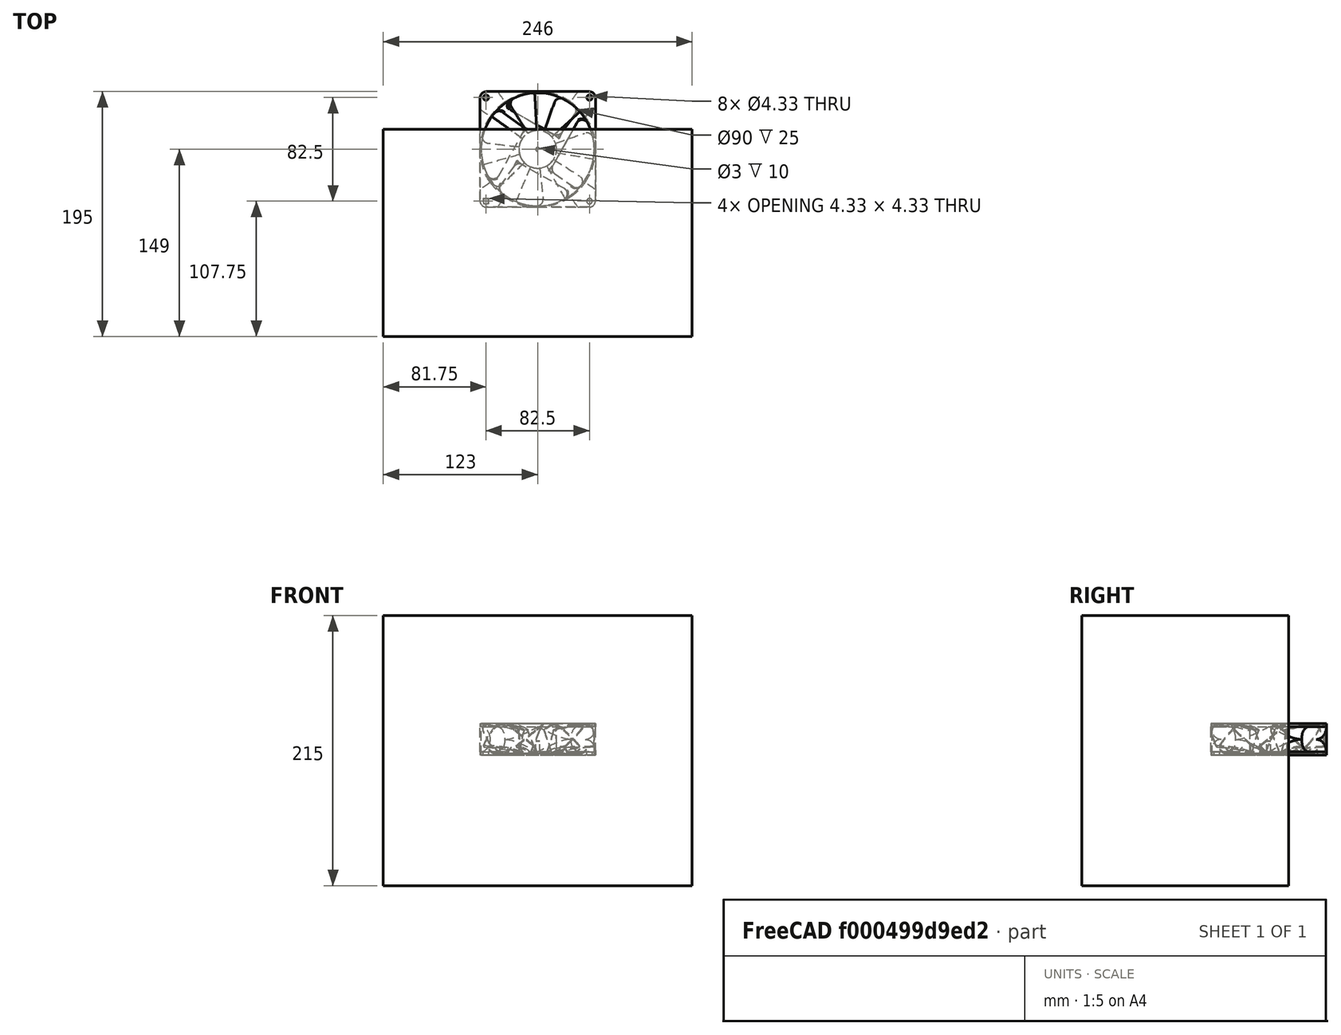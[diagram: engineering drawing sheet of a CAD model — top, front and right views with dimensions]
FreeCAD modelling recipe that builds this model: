
FCSTD DOCUMENT  (FreeCAD 0.21R33668 +7 (Git))
Label: Odroid_h4_mount_CAR_July_15_2024
License: All rights reserved
LicenseURL: https://en.wikipedia.org/wiki/All_rights_reserved
objects: Part::Box×81, Part::MultiFuse×38, Part::Cylinder×30, Part::Cut×6, Part::Feature×3, Part::Fillet×3, App::Part×2, Mesh::Feature×1
note: 161 computed .brp shape members not serialized (recipe doc carries the construction recipe); baked Part::Feature solids carry a one-line shape summary decoded from their .brp

FEATURE [Part::Feature] Part__Feature  label="fan form"
  shape: bbox 105.3 x 105.3 x 25.46 mm, 118 faces (baked)
FEATURE [Part::Feature] Part__Feature001  label="fan"
  Placement = pos=(0,0,1.25) rot=(0,0,-1;0.171016rad)
  shape: bbox 91.23 x 90.98 x 28.5 mm, 54 faces (baked)
FEATURE [App::Part] Assem1  label="Fan"
  Group = -> [Part__Feature,Part__Feature001]
  Origin = -> Origin
  Placement = pos=(0,-5.5,0) rot=(1,0,0;1.5708rad)
FEATURE [Part::Box] Box  label="Base_Plate"
  AttacherType = Attacher::AttachEngine3D
  Height = 45
  Length = 152
  Placement = pos=(76,6,-57) rot=(0,0.707107,-0.707107;3.14159rad)
  Width = 15
FEATURE [Part::Box] Box001  label="Cube001"
  AttacherType = Attacher::AttachEngine3D
  Height = 118
  Length = 11
  Placement = pos=(65,0,-57) rot=(0,0,1;0rad)
  Width = 6
FEATURE [Part::Box] Box002  label="Cube002"
  AttacherType = Attacher::AttachEngine3D
  Height = 118
  Length = 11
  Placement = pos=(-76,0,-57) rot=(0,0,1;0rad)
  Width = 6
FEATURE [Part::Feature] Part__Feature002  label="Fan_mount"
  Placement = pos=(0,0,0) rot=(-1,0,0;1.5708rad)
  shape: bbox 152 x 14.25 x 122 mm, 73 faces (baked)
FEATURE [Part::MultiFuse] Fusion  label="Base"
  Shapes = -> [Box,Box001,Box002]
FEATURE [Part::Fillet] Fillet  label="Fan_hold"
  Base = -> Fusion
  Edges = 2 edges r=2.5: [Edge7,Edge36]
FEATURE [Part::Box] Box003  label="Volume "
  AttacherType = Attacher::AttachEngine3D
  Height = 165
  Length = 246
  Placement = pos=(123,16,111) rot=(0,0.707107,-0.707107;3.14159rad)
  Width = 215
FEATURE [Mesh::Feature] Odroid_H004  label="Odroid-H004"
  Placement = pos=(-50,-110,62) rot=(1,0,0;4.71239rad)
FEATURE [Part::Box] Box004  label="Base_Plate001"
  AttacherType = Attacher::AttachEngine3D
  Height = 102
  Length = 152
  Placement = pos=(76,-39,-57) rot=(0,0.707107,-0.707107;3.14159rad)
  Width = 15
FEATURE [Part::Box] Box006  label="Cube003"
  AttacherType = Attacher::AttachEngine3D
  Height = 20
  Length = 10
  Placement = pos=(-35,-60,0) rot=(0,0,1;0.785398rad)
  Width = 10
FEATURE [Part::Box] Box007  label="Cube004"
  AttacherType = Attacher::AttachEngine3D
  Height = 20
  Length = 10
  Placement = pos=(-10,-60,0) rot=(0,0,1;0.785398rad)
  Width = 10
FEATURE [Part::Box] Box008  label="Cube005"
  AttacherType = Attacher::AttachEngine3D
  Height = 20
  Length = 10
  Placement = pos=(15,-60,0) rot=(0,0,1;0.785398rad)
  Width = 10
FEATURE [Part::Box] Box009  label="Cube006"
  AttacherType = Attacher::AttachEngine3D
  Height = 20
  Length = 10
  Placement = pos=(40,-60,0) rot=(0,0,1;0.785398rad)
  Width = 10
FEATURE [Part::Box] Box010  label="Cube007"
  AttacherType = Attacher::AttachEngine3D
  Height = 20
  Length = 10
  Placement = pos=(64,-60,0) rot=(0,0,1;0.785398rad)
  Width = 10
FEATURE [Part::Box] Box011  label="Cube008"
  AttacherType = Attacher::AttachEngine3D
  Height = 20
  Length = 10
  Placement = pos=(-60,-60,0) rot=(0,0,1;0.785398rad)
  Width = 10
FEATURE [Part::Box] Box012  label="Cube009"
  AttacherType = Attacher::AttachEngine3D
  Height = 20
  Length = 10
  Placement = pos=(-35,-60,0) rot=(0,0,1;0.785398rad)
  Width = 10
FEATURE [Part::Box] Box013  label="Cube010"
  AttacherType = Attacher::AttachEngine3D
  Height = 20
  Length = 10
  Placement = pos=(-10,-60,0) rot=(0,0,1;0.785398rad)
  Width = 10
FEATURE [Part::Box] Box014  label="Cube011"
  AttacherType = Attacher::AttachEngine3D
  Height = 20
  Length = 10
  Placement = pos=(15,-60,0) rot=(0,0,1;0.785398rad)
  Width = 10
FEATURE [Part::Box] Box015  label="Cube012"
  AttacherType = Attacher::AttachEngine3D
  Height = 20
  Length = 10
  Placement = pos=(40,-60,0) rot=(0,0,1;0.785398rad)
  Width = 10
FEATURE [Part::MultiFuse] Fusion002  label="CubeLine002"
  Placement = pos=(10,-13,0) rot=(0,0,1;0rad)
  Shapes = -> [Box011,Box012,Box013,Box014,Box015]
FEATURE [Part::Box] Box016  label="Cube013"
  AttacherType = Attacher::AttachEngine3D
  Height = 20
  Length = 10
  Placement = pos=(-60,-60,0) rot=(0,0,1;0.785398rad)
  Width = 10
FEATURE [Part::Box] Box017  label="Cube014"
  AttacherType = Attacher::AttachEngine3D
  Height = 20
  Length = 10
  Placement = pos=(-35,-60,0) rot=(0,0,1;0.785398rad)
  Width = 10
FEATURE [Part::Box] Box018  label="Cube015"
  AttacherType = Attacher::AttachEngine3D
  Height = 20
  Length = 10
  Placement = pos=(-10,-60,0) rot=(0,0,1;0.785398rad)
  Width = 10
FEATURE [Part::Box] Box019  label="Cube016"
  AttacherType = Attacher::AttachEngine3D
  Height = 20
  Length = 10
  Placement = pos=(15,-60,0) rot=(0,0,1;0.785398rad)
  Width = 10
FEATURE [Part::Box] Box020  label="Cube017"
  AttacherType = Attacher::AttachEngine3D
  Height = 20
  Length = 10
  Placement = pos=(40,-60,0) rot=(0,0,1;0.785398rad)
  Width = 10
FEATURE [Part::Box] Box021  label="Cube018"
  AttacherType = Attacher::AttachEngine3D
  Height = 20
  Length = 10
  Placement = pos=(64,-60,0) rot=(0,0,1;0.785398rad)
  Width = 10
FEATURE [Part::MultiFuse] Fusion003  label="CubeLine003"
  Placement = pos=(-2,-25,0) rot=(0,0,1;0rad)
  Shapes = -> [Box016,Box017,Box018,Box019,Box020,Box021]
FEATURE [Part::Box] Box005  label="Cube"
  AttacherType = Attacher::AttachEngine3D
  Height = 20
  Length = 10
  Placement = pos=(-60,-60,0) rot=(0,0,1;0.785398rad)
  Width = 10
FEATURE [Part::MultiFuse] Fusion001  label="CubeLine1"
  Placement = pos=(-2,0,0) rot=(0,0,1;0rad)
  Shapes = -> [Box005,Box006,Box007,Box008,Box009,Box010]
FEATURE [Part::MultiFuse] Fusion004
  Placement = pos=(0,0,-75) rot=(0,0,1;0rad)
  Shapes = -> [Fusion001,Fusion002,Fusion003]
FEATURE [Part::Cut] Cut  label="BasePlate01"
  Base = -> Box004
  Tool = -> Fusion004
FEATURE [Part::Box] Box022  label="Cube019"
  AttacherType = Attacher::AttachEngine3D
  Height = 118
  Length = 15
  Placement = pos=(49,-141,-57) rot=(0,0,1;0rad)
  Width = 10
FEATURE [Part::Box] Box023  label="Cube020"
  AttacherType = Attacher::AttachEngine3D
  Height = 118
  Length = 15
  Placement = pos=(-54,-141,-57) rot=(0,0,1;0rad)
  Width = 10
FEATURE [Part::MultiFuse] Fusion005  label="Base_H4"
  Shapes = -> [Cut,Box022,Box023]
FEATURE [Part::Cylinder] Cylinder
  Angle = 360
  AttacherType = Attacher::AttachEngine3D
  FirstAngle = 0
  Height = 20
  Placement = pos=(-46.19,-136,44.22) rot=(1,0,0;1.5708rad)
  Radius = 1.75
  SecondAngle = 0
FEATURE [Part::Cylinder] Cylinder001
  Angle = 360
  AttacherType = Attacher::AttachEngine3D
  FirstAngle = 0
  Height = 20
  Placement = pos=(-46.19,-136,-44.19) rot=(1,0,0;1.5708rad)
  Radius = 1.75
  SecondAngle = 0
FEATURE [Part::Cylinder] Cylinder002
  Angle = 360
  AttacherType = Attacher::AttachEngine3D
  FirstAngle = 0
  Height = 20
  Placement = pos=(56.05,-136,-44.2) rot=(1,0,0;1.5708rad)
  Radius = 1.75
  SecondAngle = 0
FEATURE [Part::Cylinder] Cylinder003
  Angle = 360
  AttacherType = Attacher::AttachEngine3D
  FirstAngle = 0
  Height = 20
  Placement = pos=(56.05,-136,37.23) rot=(1,0,0;1.5708rad)
  Radius = 1.75
  SecondAngle = 0
FEATURE [Part::MultiFuse] Fusion006  label="Mount_cut"
  Placement = pos=(0,10,0) rot=(0,0,1;0rad)
  Shapes = -> [Cylinder,Cylinder001,Cylinder002,Cylinder003]
FEATURE [Part::Cut] Cut001  label="h4_mount"
  Base = -> Fusion005
  Tool = -> Fusion006
FEATURE [Part::MultiFuse] Fusion007  label="Mount01"
  Shapes = -> [Cut001,Fillet,Part__Feature002]
FEATURE [Part::Fillet] Fillet001  label="Mount"
  Base = -> Fusion007
  Edges = 17 edges r=1: [Edge182,Edge183,Edge184,Edge187,Edge188,Edge307,Edge308,Edge309,Edge310,Edge314,Edge316,Edge317,Edge318,Edge319,Edge323,Edge461,Edge464]
FEATURE [Part::Cylinder] Cylinder004
  Angle = 360
  AttacherType = Attacher::AttachEngine3D
  FirstAngle = 0
  Height = 30
  Placement = pos=(70,17,54) rot=(1,0,0;1.5708rad)
  Radius = 1.75
  SecondAngle = 0
FEATURE [Part::Cylinder] Cylinder005
  Angle = 360
  AttacherType = Attacher::AttachEngine3D
  FirstAngle = 0
  Height = 30
  Placement = pos=(-70,17,54) rot=(1,0,0;1.5708rad)
  Radius = 1.75
  SecondAngle = 0
FEATURE [Part::Cylinder] Cylinder006
  Angle = 360
  AttacherType = Attacher::AttachEngine3D
  FirstAngle = 0
  Height = 30
  Placement = pos=(70,18,-52) rot=(1,0,0;1.5708rad)
  Radius = 1.75
  SecondAngle = 0
FEATURE [Part::Cylinder] Cylinder007
  Angle = 360
  AttacherType = Attacher::AttachEngine3D
  FirstAngle = 0
  Height = 30
  Placement = pos=(-70,18,-52) rot=(1,0,0;1.5708rad)
  Radius = 1.75
  SecondAngle = 0
FEATURE [Part::MultiFuse] Fusion008  label="m3_mount_Cut"
  Shapes = -> [Cylinder004,Cylinder005,Cylinder006,Cylinder007]
FEATURE [Part::Cylinder] Cylinder008
  Angle = 360
  AttacherType = Attacher::AttachEngine3D
  FirstAngle = 0
  Height = 20
  Placement = pos=(70,17,54) rot=(1,0,0;1.5708rad)
  Radius = 3
  SecondAngle = 0
FEATURE [Part::Cylinder] Cylinder009
  Angle = 360
  AttacherType = Attacher::AttachEngine3D
  FirstAngle = 0
  Height = 20
  Placement = pos=(-70,17,54) rot=(1,0,0;1.5708rad)
  Radius = 3
  SecondAngle = 0
FEATURE [Part::Cylinder] Cylinder010
  Angle = 360
  AttacherType = Attacher::AttachEngine3D
  FirstAngle = 0
  Height = 20
  Placement = pos=(70,18,-52) rot=(1,0,0;1.5708rad)
  Radius = 3
  SecondAngle = 0
FEATURE [Part::Cylinder] Cylinder011
  Angle = 360
  AttacherType = Attacher::AttachEngine3D
  FirstAngle = 0
  Height = 20
  Placement = pos=(-70,18,-52) rot=(1,0,0;1.5708rad)
  Radius = 3
  SecondAngle = 0
FEATURE [Part::MultiFuse] Fusion009  label="m3_mount_support"
  Placement = pos=(0,-6,0) rot=(0,0,1;0rad)
  Shapes = -> [Cylinder008,Cylinder009,Cylinder010,Cylinder011]
FEATURE [Part::MultiFuse] Fusion010  label="Mount002"
  Shapes = -> [Fillet001,Fusion009]
FEATURE [Part::Cut] Cut002  label="Base001"
  Base = -> Fusion010
  Tool = -> Fusion008
FEATURE [Part::Box] Box024  label="Base_Plate002"
  AttacherType = Attacher::AttachEngine3D
  Height = 134
  Length = 147
  Placement = pos=(76,72,6) rot=(0.57735,0.57735,-0.57735;2.0944rad)
  Width = 15
FEATURE [Part::Box] Box025  label="Base_Plate003"
  AttacherType = Attacher::AttachEngine3D
  Height = 134
  Length = 147
  Placement = pos=(-76,72,-141) rot=(0.57735,-0.57735,0.57735;2.0944rad)
  Width = 15
FEATURE [Part::Box] Box027  label="Cube022"
  AttacherType = Attacher::AttachEngine3D
  Height = 20
  Length = 10
  Placement = pos=(-35,-60,0) rot=(0,0,1;0.785398rad)
  Width = 10
FEATURE [Part::Box] Box028  label="Cube023"
  AttacherType = Attacher::AttachEngine3D
  Height = 20
  Length = 10
  Placement = pos=(-10,-60,0) rot=(0,0,1;0.785398rad)
  Width = 10
FEATURE [Part::Box] Box029  label="Cube024"
  AttacherType = Attacher::AttachEngine3D
  Height = 20
  Length = 10
  Placement = pos=(15,-60,0) rot=(0,0,1;0.785398rad)
  Width = 10
FEATURE [Part::Box] Box030  label="Cube025"
  AttacherType = Attacher::AttachEngine3D
  Height = 20
  Length = 10
  Placement = pos=(40,-60,0) rot=(0,0,1;0.785398rad)
  Width = 10
FEATURE [Part::Box] Box032  label="Cube027"
  AttacherType = Attacher::AttachEngine3D
  Height = 20
  Length = 10
  Placement = pos=(-60,-60,0) rot=(0,0,1;0.785398rad)
  Width = 10
FEATURE [Part::Box] Box033  label="Cube028"
  AttacherType = Attacher::AttachEngine3D
  Height = 20
  Length = 10
  Placement = pos=(-35,-60,0) rot=(0,0,1;0.785398rad)
  Width = 10
FEATURE [Part::Box] Box034  label="Cube029"
  AttacherType = Attacher::AttachEngine3D
  Height = 20
  Length = 10
  Placement = pos=(-10,-60,0) rot=(0,0,1;0.785398rad)
  Width = 10
FEATURE [Part::Box] Box035  label="Cube030"
  AttacherType = Attacher::AttachEngine3D
  Height = 20
  Length = 10
  Placement = pos=(15,-60,0) rot=(0,0,1;0.785398rad)
  Width = 10
FEATURE [Part::Box] Box036  label="Cube031"
  AttacherType = Attacher::AttachEngine3D
  Height = 20
  Length = 10
  Placement = pos=(40,-60,0) rot=(0,0,1;0.785398rad)
  Width = 10
FEATURE [Part::Box] Box038  label="Cube033"
  AttacherType = Attacher::AttachEngine3D
  Height = 20
  Length = 10
  Placement = pos=(-35,-60,0) rot=(0,0,1;0.785398rad)
  Width = 10
FEATURE [Part::Box] Box039  label="Cube034"
  AttacherType = Attacher::AttachEngine3D
  Height = 20
  Length = 10
  Placement = pos=(-10,-60,0) rot=(0,0,1;0.785398rad)
  Width = 10
FEATURE [Part::Box] Box040  label="Cube035"
  AttacherType = Attacher::AttachEngine3D
  Height = 20
  Length = 10
  Placement = pos=(15,-60,0) rot=(0,0,1;0.785398rad)
  Width = 10
FEATURE [Part::Box] Box041  label="Cube036"
  AttacherType = Attacher::AttachEngine3D
  Height = 20
  Length = 10
  Placement = pos=(40,-60,0) rot=(0,0,1;0.785398rad)
  Width = 10
FEATURE [Part::MultiFuse] Fusion011  label="CubeLine004"
  Placement = pos=(-2,0,0) rot=(0,0,1;0rad)
  Shapes = -> [Box027,Box028,Box029,Box030]
FEATURE [Part::MultiFuse] Fusion012  label="CubeLine005"
  Placement = pos=(10,-13,0) rot=(0,0,1;0rad)
  Shapes = -> [Box032,Box033,Box034,Box035,Box036]
FEATURE [Part::MultiFuse] Fusion013  label="CubeLine006"
  Placement = pos=(-2,-25,0) rot=(0,0,1;0rad)
  Shapes = -> [Box038,Box039,Box040,Box041]
FEATURE [Part::MultiFuse] Fusion014
  Placement = pos=(94,95,-68) rot=(0,1,0;4.71239rad)
  Shapes = -> [Fusion011,Fusion012,Fusion013]
FEATURE [Part::Box] Box044  label="Cube039"
  AttacherType = Attacher::AttachEngine3D
  Height = 20
  Length = 10
  Placement = pos=(-35,-60,0) rot=(0,0,1;0.785398rad)
  Width = 10
FEATURE [Part::Box] Box045  label="Cube040"
  AttacherType = Attacher::AttachEngine3D
  Height = 20
  Length = 10
  Placement = pos=(-10,-60,0) rot=(0,0,1;0.785398rad)
  Width = 10
FEATURE [Part::Box] Box046  label="Cube041"
  AttacherType = Attacher::AttachEngine3D
  Height = 20
  Length = 10
  Placement = pos=(15,-60,0) rot=(0,0,1;0.785398rad)
  Width = 10
FEATURE [Part::Box] Box047  label="Cube042"
  AttacherType = Attacher::AttachEngine3D
  Height = 20
  Length = 10
  Placement = pos=(40,-60,0) rot=(0,0,1;0.785398rad)
  Width = 10
FEATURE [Part::Box] Box049  label="Cube044"
  AttacherType = Attacher::AttachEngine3D
  Height = 20
  Length = 10
  Placement = pos=(-60,-60,0) rot=(0,0,1;0.785398rad)
  Width = 10
FEATURE [Part::Box] Box050  label="Cube045"
  AttacherType = Attacher::AttachEngine3D
  Height = 20
  Length = 10
  Placement = pos=(-35,-60,0) rot=(0,0,1;0.785398rad)
  Width = 10
FEATURE [Part::Box] Box051  label="Cube046"
  AttacherType = Attacher::AttachEngine3D
  Height = 20
  Length = 10
  Placement = pos=(-10,-60,0) rot=(0,0,1;0.785398rad)
  Width = 10
FEATURE [Part::Box] Box052  label="Cube047"
  AttacherType = Attacher::AttachEngine3D
  Height = 20
  Length = 10
  Placement = pos=(15,-60,0) rot=(0,0,1;0.785398rad)
  Width = 10
FEATURE [Part::Box] Box053  label="Cube048"
  AttacherType = Attacher::AttachEngine3D
  Height = 20
  Length = 10
  Placement = pos=(40,-60,0) rot=(0,0,1;0.785398rad)
  Width = 10
FEATURE [Part::Box] Box055  label="Cube050"
  AttacherType = Attacher::AttachEngine3D
  Height = 20
  Length = 10
  Placement = pos=(-35,-60,0) rot=(0,0,1;0.785398rad)
  Width = 10
FEATURE [Part::Box] Box056  label="Cube051"
  AttacherType = Attacher::AttachEngine3D
  Height = 20
  Length = 10
  Placement = pos=(-10,-60,0) rot=(0,0,1;0.785398rad)
  Width = 10
FEATURE [Part::Box] Box057  label="Cube052"
  AttacherType = Attacher::AttachEngine3D
  Height = 20
  Length = 10
  Placement = pos=(15,-60,0) rot=(0,0,1;0.785398rad)
  Width = 10
FEATURE [Part::Box] Box058  label="Cube053"
  AttacherType = Attacher::AttachEngine3D
  Height = 20
  Length = 10
  Placement = pos=(40,-60,0) rot=(0,0,1;0.785398rad)
  Width = 10
FEATURE [Part::MultiFuse] Fusion015  label="CubeLine007"
  Placement = pos=(-2,0,0) rot=(0,0,1;0rad)
  Shapes = -> [Box044,Box045,Box046,Box047]
FEATURE [Part::MultiFuse] Fusion016  label="CubeLine008"
  Placement = pos=(10,-13,0) rot=(0,0,1;0rad)
  Shapes = -> [Box049,Box050,Box051,Box052,Box053]
FEATURE [Part::MultiFuse] Fusion017  label="CubeLine009"
  Placement = pos=(-2,-25,0) rot=(0,0,1;0rad)
  Shapes = -> [Box055,Box056,Box057,Box058]
FEATURE [Part::MultiFuse] Fusion018
  Placement = pos=(94,45,-68) rot=(0,-1,0;1.5708rad)
  Shapes = -> [Fusion015,Fusion016,Fusion017]
FEATURE [Part::MultiFuse] Fusion019  label="Cube_Cut_Side1"
  Shapes = -> [Fusion014,Fusion018]
FEATURE [Part::Cut] Cut003  label="side1"
  Base = -> Box024
  Placement = pos=(0,0,0) rot=(1,0,0;4.71239rad)
  Tool = -> Fusion019
FEATURE [Part::Box] Box061  label="Cube056"
  AttacherType = Attacher::AttachEngine3D
  Height = 20
  Length = 10
  Placement = pos=(-35,-60,0) rot=(0,0,1;0.785398rad)
  Width = 10
FEATURE [Part::Box] Box062  label="Cube057"
  AttacherType = Attacher::AttachEngine3D
  Height = 20
  Length = 10
  Placement = pos=(-10,-60,0) rot=(0,0,1;0.785398rad)
  Width = 10
FEATURE [Part::Box] Box063  label="Cube058"
  AttacherType = Attacher::AttachEngine3D
  Height = 20
  Length = 10
  Placement = pos=(15,-60,0) rot=(0,0,1;0.785398rad)
  Width = 10
FEATURE [Part::Box] Box064  label="Cube059"
  AttacherType = Attacher::AttachEngine3D
  Height = 20
  Length = 10
  Placement = pos=(40,-60,0) rot=(0,0,1;0.785398rad)
  Width = 10
FEATURE [Part::Box] Box066  label="Cube061"
  AttacherType = Attacher::AttachEngine3D
  Height = 20
  Length = 10
  Placement = pos=(-60,-60,0) rot=(0,0,1;0.785398rad)
  Width = 10
FEATURE [Part::Box] Box067  label="Cube062"
  AttacherType = Attacher::AttachEngine3D
  Height = 20
  Length = 10
  Placement = pos=(-35,-60,0) rot=(0,0,1;0.785398rad)
  Width = 10
FEATURE [Part::Box] Box068  label="Cube063"
  AttacherType = Attacher::AttachEngine3D
  Height = 20
  Length = 10
  Placement = pos=(-10,-60,0) rot=(0,0,1;0.785398rad)
  Width = 10
FEATURE [Part::Box] Box069  label="Cube064"
  AttacherType = Attacher::AttachEngine3D
  Height = 20
  Length = 10
  Placement = pos=(15,-60,0) rot=(0,0,1;0.785398rad)
  Width = 10
FEATURE [Part::Box] Box070  label="Cube065"
  AttacherType = Attacher::AttachEngine3D
  Height = 20
  Length = 10
  Placement = pos=(40,-60,0) rot=(0,0,1;0.785398rad)
  Width = 10
FEATURE [Part::Box] Box072  label="Cube067"
  AttacherType = Attacher::AttachEngine3D
  Height = 20
  Length = 10
  Placement = pos=(-35,-60,0) rot=(0,0,1;0.785398rad)
  Width = 10
FEATURE [Part::Box] Box073  label="Cube068"
  AttacherType = Attacher::AttachEngine3D
  Height = 20
  Length = 10
  Placement = pos=(-10,-60,0) rot=(0,0,1;0.785398rad)
  Width = 10
FEATURE [Part::Box] Box074  label="Cube069"
  AttacherType = Attacher::AttachEngine3D
  Height = 20
  Length = 10
  Placement = pos=(15,-60,0) rot=(0,0,1;0.785398rad)
  Width = 10
FEATURE [Part::Box] Box075  label="Cube070"
  AttacherType = Attacher::AttachEngine3D
  Height = 20
  Length = 10
  Placement = pos=(40,-60,0) rot=(0,0,1;0.785398rad)
  Width = 10
FEATURE [Part::Box] Box078  label="Cube073"
  AttacherType = Attacher::AttachEngine3D
  Height = 20
  Length = 10
  Placement = pos=(-35,-60,0) rot=(0,0,1;0.785398rad)
  Width = 10
FEATURE [Part::Box] Box079  label="Cube074"
  AttacherType = Attacher::AttachEngine3D
  Height = 20
  Length = 10
  Placement = pos=(-10,-60,0) rot=(0,0,1;0.785398rad)
  Width = 10
FEATURE [Part::Box] Box080  label="Cube075"
  AttacherType = Attacher::AttachEngine3D
  Height = 20
  Length = 10
  Placement = pos=(15,-60,0) rot=(0,0,1;0.785398rad)
  Width = 10
FEATURE [Part::Box] Box081  label="Cube076"
  AttacherType = Attacher::AttachEngine3D
  Height = 20
  Length = 10
  Placement = pos=(40,-60,0) rot=(0,0,1;0.785398rad)
  Width = 10
FEATURE [Part::Box] Box083  label="Cube078"
  AttacherType = Attacher::AttachEngine3D
  Height = 20
  Length = 10
  Placement = pos=(-60,-60,0) rot=(0,0,1;0.785398rad)
  Width = 10
FEATURE [Part::Box] Box084  label="Cube079"
  AttacherType = Attacher::AttachEngine3D
  Height = 20
  Length = 10
  Placement = pos=(-35,-60,0) rot=(0,0,1;0.785398rad)
  Width = 10
FEATURE [Part::Box] Box085  label="Cube080"
  AttacherType = Attacher::AttachEngine3D
  Height = 20
  Length = 10
  Placement = pos=(-10,-60,0) rot=(0,0,1;0.785398rad)
  Width = 10
FEATURE [Part::Box] Box086  label="Cube081"
  AttacherType = Attacher::AttachEngine3D
  Height = 20
  Length = 10
  Placement = pos=(15,-60,0) rot=(0,0,1;0.785398rad)
  Width = 10
FEATURE [Part::Box] Box087  label="Cube082"
  AttacherType = Attacher::AttachEngine3D
  Height = 20
  Length = 10
  Placement = pos=(40,-60,0) rot=(0,0,1;0.785398rad)
  Width = 10
FEATURE [Part::Box] Box089  label="Cube084"
  AttacherType = Attacher::AttachEngine3D
  Height = 20
  Length = 10
  Placement = pos=(-35,-60,0) rot=(0,0,1;0.785398rad)
  Width = 10
FEATURE [Part::Box] Box090  label="Cube085"
  AttacherType = Attacher::AttachEngine3D
  Height = 20
  Length = 10
  Placement = pos=(-10,-60,0) rot=(0,0,1;0.785398rad)
  Width = 10
FEATURE [Part::Box] Box091  label="Cube086"
  AttacherType = Attacher::AttachEngine3D
  Height = 20
  Length = 10
  Placement = pos=(15,-60,0) rot=(0,0,1;0.785398rad)
  Width = 10
FEATURE [Part::Box] Box092  label="Cube087"
  AttacherType = Attacher::AttachEngine3D
  Height = 20
  Length = 10
  Placement = pos=(40,-60,0) rot=(0,0,1;0.785398rad)
  Width = 10
FEATURE [Part::MultiFuse] Fusion020  label="CubeLine010"
  Placement = pos=(-2,0,0) rot=(0,0,1;0rad)
  Shapes = -> [Box061,Box062,Box063,Box064]
FEATURE [Part::MultiFuse] Fusion021  label="CubeLine011"
  Placement = pos=(10,-13,0) rot=(0,0,1;0rad)
  Shapes = -> [Box066,Box067,Box068,Box069,Box070]
FEATURE [Part::MultiFuse] Fusion022  label="CubeLine012"
  Placement = pos=(-2,-25,0) rot=(0,0,1;0rad)
  Shapes = -> [Box072,Box073,Box074,Box075]
FEATURE [Part::MultiFuse] Fusion023
  Placement = pos=(94,95,-68) rot=(0,-1,0;1.5708rad)
  Shapes = -> [Fusion020,Fusion021,Fusion022]
FEATURE [Part::MultiFuse] Fusion024  label="CubeLine013"
  Placement = pos=(-2,0,0) rot=(0,0,1;0rad)
  Shapes = -> [Box078,Box079,Box080,Box081]
FEATURE [Part::MultiFuse] Fusion025  label="CubeLine014"
  Placement = pos=(10,-13,0) rot=(0,0,1;0rad)
  Shapes = -> [Box083,Box084,Box085,Box086,Box087]
FEATURE [Part::MultiFuse] Fusion026  label="CubeLine015"
  Placement = pos=(-2,-25,0) rot=(0,0,1;0rad)
  Shapes = -> [Box089,Box090,Box091,Box092]
FEATURE [Part::MultiFuse] Fusion027
  Placement = pos=(94,45,-68) rot=(0,-1,0;1.5708rad)
  Shapes = -> [Fusion024,Fusion025,Fusion026]
FEATURE [Part::MultiFuse] Fusion028  label="Cube_Cut_Side2"
  Placement = pos=(-167,0,0) rot=(0,0,1;0rad)
  Shapes = -> [Fusion023,Fusion027]
FEATURE [Part::Cut] Cut004  label="side2"
  Base = -> Box025
  Placement = pos=(0,0,0) rot=(1,0,0;4.71239rad)
  Tool = -> Fusion028
FEATURE [Part::Box] Box094  label="MountPLate1"
  AttacherType = Attacher::AttachEngine3D
  Height = 134
  Length = 30
  Placement = pos=(91,-141,-72) rot=(0,0,1;0rad)
  Width = 10
FEATURE [Part::Box] Box095  label="MountPLate002"
  AttacherType = Attacher::AttachEngine3D
  Height = 134
  Length = 30
  Placement = pos=(-121,-141,-72) rot=(0,0,1;0rad)
  Width = 10
FEATURE [Part::Box] Box096  label="MountPLate003"
  AttacherType = Attacher::AttachEngine3D
  Height = 182
  Length = 30
  Placement = pos=(91,-141,-102) rot=(0,1,0;4.71239rad)
  Width = 10
FEATURE [Part::MultiFuse] Fusion029  label="Mount001"
  Shapes = -> [Cut002,Box094,Cut003,Cut004,Box095,Box096]
FEATURE [Part::Fillet] Fillet002
  Base = -> Fusion029
  Edges = 15 edges r=2.5: [Edge2,Edge4,Edge11,Edge12,Edge18,Edge20,Edge126,Edge367,Edge523,Edge603,Edge825,Edge826,Edge915,Edge927,Edge1160]
FEATURE [Part::Cylinder] Cylinder012
  Angle = 360
  AttacherType = Attacher::AttachEngine3D
  FirstAngle = 0
  Height = 10
  Placement = pos=(0,-136,-86) rot=(1,0,0;4.71239rad)
  Radius = 3
  SecondAngle = 0
FEATURE [Part::Cylinder] Cylinder013
  Angle = 360
  AttacherType = Attacher::AttachEngine3D
  FirstAngle = 0
  Height = 10
  Placement = pos=(-70,-136,-86) rot=(-1,0,0;1.5708rad)
  Radius = 3
  SecondAngle = 0
FEATURE [Part::Cylinder] Cylinder014
  Angle = 360
  AttacherType = Attacher::AttachEngine3D
  FirstAngle = 0
  Height = 10
  Placement = pos=(70,-136,-86) rot=(-1,0,0;1.5708rad)
  Radius = 3
  SecondAngle = 0
FEATURE [Part::Cylinder] Cylinder015
  Angle = 360
  AttacherType = Attacher::AttachEngine3D
  FirstAngle = 0
  Height = 10
  Placement = pos=(107,-136,-59) rot=(-1,0,0;1.5708rad)
  Radius = 3
  SecondAngle = 0
FEATURE [Part::Cylinder] Cylinder016
  Angle = 360
  AttacherType = Attacher::AttachEngine3D
  FirstAngle = 0
  Height = 10
  Placement = pos=(107,-136,49) rot=(-1,0,0;1.5708rad)
  Radius = 3
  SecondAngle = 0
FEATURE [Part::Cylinder] Cylinder017
  Angle = 360
  AttacherType = Attacher::AttachEngine3D
  FirstAngle = 0
  Height = 10
  Placement = pos=(107,-136,-5) rot=(-1,0,0;1.5708rad)
  Radius = 3
  SecondAngle = 0
FEATURE [Part::MultiFuse] Fusion030  label="side_m3_support"
  Shapes = -> [Cylinder015,Cylinder016,Cylinder017]
FEATURE [Part::Cylinder] Cylinder018
  Angle = 360
  AttacherType = Attacher::AttachEngine3D
  FirstAngle = 0
  Height = 10
  Placement = pos=(107,-136,-59) rot=(-1,0,0;1.5708rad)
  Radius = 3
  SecondAngle = 0
FEATURE [Part::Cylinder] Cylinder019
  Angle = 360
  AttacherType = Attacher::AttachEngine3D
  FirstAngle = 0
  Height = 10
  Placement = pos=(107,-136,49) rot=(-1,0,0;1.5708rad)
  Radius = 3
  SecondAngle = 0
FEATURE [Part::Cylinder] Cylinder020
  Angle = 360
  AttacherType = Attacher::AttachEngine3D
  FirstAngle = 0
  Height = 10
  Placement = pos=(107,-136,-5) rot=(-1,0,0;1.5708rad)
  Radius = 3
  SecondAngle = 0
FEATURE [Part::MultiFuse] Fusion031  label="side_m3_support001"
  Placement = pos=(-214,0,0) rot=(0,0,1;0rad)
  Shapes = -> [Cylinder018,Cylinder019,Cylinder020]
FEATURE [Part::Cylinder] Cylinder021
  Angle = 360
  AttacherType = Attacher::AttachEngine3D
  FirstAngle = 0
  Height = 30
  Placement = pos=(107,-136,-59) rot=(-1,0,0;1.5708rad)
  Radius = 1.75
  SecondAngle = 0
FEATURE [Part::Cylinder] Cylinder022
  Angle = 360
  AttacherType = Attacher::AttachEngine3D
  FirstAngle = 0
  Height = 30
  Placement = pos=(107,-136,49) rot=(-1,0,0;1.5708rad)
  Radius = 1.75
  SecondAngle = 0
FEATURE [Part::Cylinder] Cylinder023
  Angle = 360
  AttacherType = Attacher::AttachEngine3D
  FirstAngle = 0
  Height = 30
  Placement = pos=(107,-136,-5) rot=(-1,0,0;1.5708rad)
  Radius = 1.75
  SecondAngle = 0
FEATURE [Part::MultiFuse] Fusion032  label="side_m3_hole"
  Placement = pos=(0,-15,0) rot=(0,0,1;0rad)
  Shapes = -> [Cylinder021,Cylinder022,Cylinder023]
FEATURE [Part::Cylinder] Cylinder024
  Angle = 360
  AttacherType = Attacher::AttachEngine3D
  FirstAngle = 0
  Height = 30
  Placement = pos=(107,-136,-59) rot=(-1,0,0;1.5708rad)
  Radius = 1.75
  SecondAngle = 0
FEATURE [Part::Cylinder] Cylinder025
  Angle = 360
  AttacherType = Attacher::AttachEngine3D
  FirstAngle = 0
  Height = 30
  Placement = pos=(107,-136,49) rot=(-1,0,0;1.5708rad)
  Radius = 1.75
  SecondAngle = 0
FEATURE [Part::Cylinder] Cylinder026
  Angle = 360
  AttacherType = Attacher::AttachEngine3D
  FirstAngle = 0
  Height = 30
  Placement = pos=(107,-136,-5) rot=(-1,0,0;1.5708rad)
  Radius = 1.75
  SecondAngle = 0
FEATURE [Part::MultiFuse] Fusion033  label="side_m3_hole001"
  Placement = pos=(-214,-15,0) rot=(0,0,1;0rad)
  Shapes = -> [Cylinder024,Cylinder025,Cylinder026]
FEATURE [Part::MultiFuse] Fusion034  label="Back_m3_support"
  Shapes = -> [Cylinder012,Cylinder013,Cylinder014]
FEATURE [Part::Cylinder] Cylinder027
  Angle = 360
  AttacherType = Attacher::AttachEngine3D
  FirstAngle = 0
  Height = 30
  Placement = pos=(0,-136,-86) rot=(-1,0,0;1.5708rad)
  Radius = 1.75
  SecondAngle = 0
FEATURE [Part::Cylinder] Cylinder028
  Angle = 360
  AttacherType = Attacher::AttachEngine3D
  FirstAngle = 0
  Height = 30
  Placement = pos=(-70,-136,-86) rot=(-1,0,0;1.5708rad)
  Radius = 1.75
  SecondAngle = 0
FEATURE [Part::Cylinder] Cylinder029
  Angle = 360
  AttacherType = Attacher::AttachEngine3D
  FirstAngle = 0
  Height = 30
  Placement = pos=(70,-136,-86) rot=(-1,0,0;1.5708rad)
  Radius = 1.75
  SecondAngle = 0
FEATURE [Part::MultiFuse] Fusion035  label="Back_m3_hole"
  Placement = pos=(0,-15,0) rot=(0,0,1;0rad)
  Shapes = -> [Cylinder027,Cylinder028,Cylinder029]
FEATURE [Part::MultiFuse] Fusion036  label="Hold_Mount"
  Shapes = -> [Fillet002,Fusion030,Fusion031,Fusion034]
FEATURE [Part::MultiFuse] Fusion037  label="m3_hole"
  Shapes = -> [Fusion032,Fusion033,Fusion035]
FEATURE [Part::Cut] Cut005  label="Mounting"
  Base = -> Fusion036
  Tool = -> Fusion037
FEATURE [App::Part] Part  label="H4_Mount"
  Group = -> [Assem1,Box003,Odroid_H004,Box021,Box020,Box017,Box005,Box022,Box023,Box019,Box052,Box018,Fillet001,Fillet,Fillet002,Fusion003,Fusion004,Cut,Fusion005,Fusion007,Cut001,Fusion008,Fusion006,Fusion009,Fusion,Fusion010,Cut002,Fusion001,Fusion002,Part__Feature002,Box,Box001,Box002,Box004,Box006,Box007,Box008,Box009,Box010,Box011,Box012,Box013,Box014,Box015,Box016,Cylinder,Cylinder001,Cylinder002,+113 more]
  Origin = -> Origin001
  Placement = pos=(0,0,0) rot=(1,0,0;1.5708rad)
